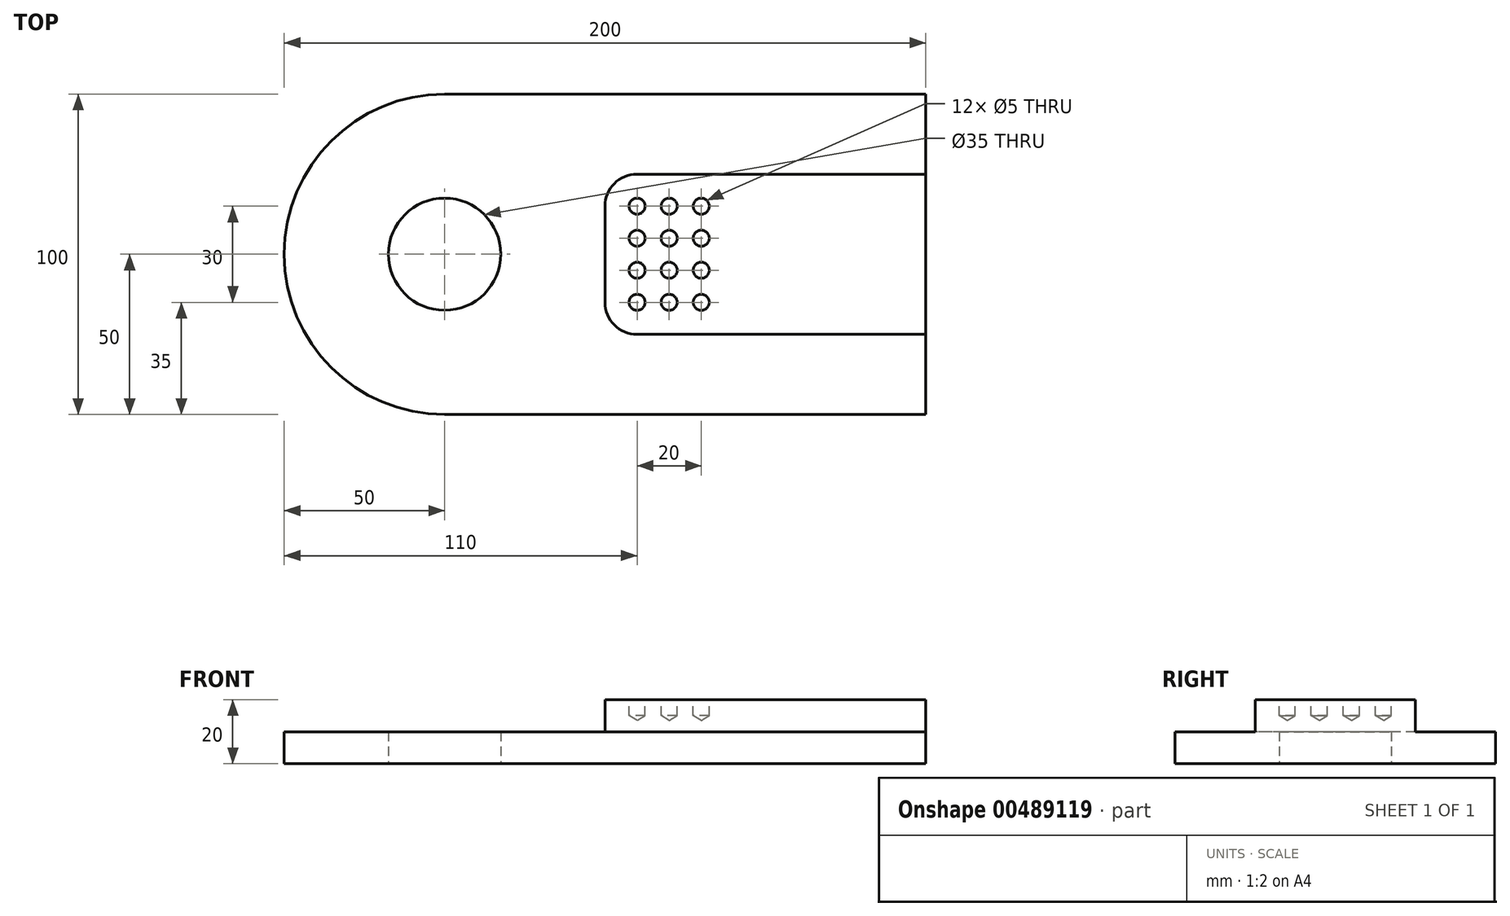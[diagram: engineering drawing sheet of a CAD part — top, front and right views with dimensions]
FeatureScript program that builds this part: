
annotation { "Feature Type Name" : "Feature", "Feature Type Description" : "" }
export const myFeature = defineFeature(function(context is Context, id is Id, definition is map)
    precondition{}
    {
        {
            var Q0;
            Q0=qCreatedBy(makeId("Top.planeOp"),FACE);
            var sketch = newSketch(context, id + "F0", { "sketchPlane" : qUnion([Q0])});
            skCircle(sketch, "E0", {"center": v(0, 0) * mm, "radius": 17.5 * mm});
            skArc(sketch, "E1", {"start": v(0, 50) * mm, "mid": v(-50, 0) * mm, "end": v(0, -50) * mm});
            skLineSegment(sketch, "E2.bottom", {"start": v(0, 50) * mm, "end": v(150, 50) * mm});
            skLineSegment(sketch, "E2.top", {"start": v(0, -50) * mm, "end": v(150, -50) * mm});
            skLineSegment(sketch, "E2.left", {"start": v(0, 50) * mm, "end": v(0, -50) * mm});
            skLineSegment(sketch, "E2.right", {"start": v(150, 50) * mm, "end": v(150, -50) * mm});
            skSolve(sketch);
        }
        {
            var Q0;
            Q0 = qSketchRegion(id + "F0", true);
            extrude(context, id + "F1", {"entities" : qUnion([Q0]), "depth" : 10 * mm});
        }
        {
            var Q0;
            Q0=makeQuery(id+"F1.opExtrude","CAP_FACE",FACE,{"disambiguationData":[OSD([sQuery(id+"F0.wireOp",EDGE,"E0"),sQuery(id+"F0.wireOp",EDGE,"E1"),sQuery(id+"F0.wireOp",EDGE,"E2.bottom"),sQuery(id+"F0.wireOp",EDGE,"E2.top"),sQuery(id+"F0.wireOp",EDGE,"E2.right")])],"isStart":false});
            var sketch = newSketch(context, id + "F2", { "sketchPlane" : qUnion([Q0])});
            skLineSegment(sketch, "E3.bottom", {"start": v(150, 25) * mm, "end": v(60, 25) * mm});
            skLineSegment(sketch, "E3.top", {"start": v(150, -25) * mm, "end": v(60, -25) * mm});
            skLineSegment(sketch, "E3.left", {"start": v(150, 25) * mm, "end": v(150, -25) * mm});
            skLineSegment(sketch, "E3.right", {"start": v(50, 15) * mm, "end": v(50, -15) * mm});
            skPoint(sketch, "E4.visualSharp", {"position": v(50, 25) * mm});
            skArc(sketch, "E4.filletArc", {"start": v(60, 25) * mm, "mid": v(52.93, 22.07) * mm, "end": v(50, 15) * mm});
            skPoint(sketch, "E5.visualSharp", {"position": v(50, -25) * mm});
            skArc(sketch, "E5.filletArc", {"start": v(50, -15) * mm, "mid": v(52.93, -22.07) * mm, "end": v(60, -25) * mm});
            skSolve(sketch);
        }
        {
            var Q0;
            Q0 = qSketchRegion(id + "F2", true);
            extrude(context, id + "F3", {"entities" : qUnion([Q0]), "operationType" : NewBodyOperationType.ADD, "depth" : 10 * mm});
        }
        {
            var Q0;
            Q0=makeQuery(id+"F3.opExtrude","CAP_FACE",FACE,{"disambiguationData":[OSD([sQuery(id+"F2.wireOp",EDGE,"E3.bottom"),sQuery(id+"F2.wireOp",EDGE,"E3.top"),sQuery(id+"F2.wireOp",EDGE,"E3.left"),sQuery(id+"F2.wireOp",EDGE,"E3.right"),sQuery(id+"F2.wireOp",EDGE,"E4.filletArc"),sQuery(id+"F2.wireOp",EDGE,"E5.filletArc")])],"isStart":false});
            var sketch = newSketch(context, id + "F4", { "sketchPlane" : qUnion([Q0])});
            skPoint(sketch, "E6", {"position": v(60, 15) * mm});
            skPoint(sketch, "E7.0.1.0", {"position": v(60, 5) * mm});
            skPoint(sketch, "E7.0.2.0", {"position": v(60, -5) * mm});
            skPoint(sketch, "E7.0.3.0", {"position": v(60, -15) * mm});
            skPoint(sketch, "E7.1.0.0", {"position": v(70, 15) * mm});
            skPoint(sketch, "E7.1.1.0", {"position": v(70, 5) * mm});
            skPoint(sketch, "E7.1.2.0", {"position": v(70, -5) * mm});
            skPoint(sketch, "E7.1.3.0", {"position": v(70, -15) * mm});
            skPoint(sketch, "E7.2.0.0", {"position": v(80, 15) * mm});
            skPoint(sketch, "E7.2.1.0", {"position": v(80, 5) * mm});
            skPoint(sketch, "E7.2.2.0", {"position": v(80, -5) * mm});
            skPoint(sketch, "E7.2.3.0", {"position": v(80, -15) * mm});
            skLineSegment(sketch, "E7.direction1", {"start": v(60, 15) * mm, "end": v(70, 15) * mm, "construction": true});
            skLineSegment(sketch, "E7.direction2", {"start": v(60, 15) * mm, "end": v(60, 5) * mm, "construction": true});
            skSolve(sketch);
        }
        {
            var Q0;
            Q0=sQuery(id+"F4.wireOp",VERTEX,"E6");
            var Q1;
            Q1=sQuery(id+"F4.wireOp",VERTEX,"E7.1.0.0");
            var Q2;
            Q2=sQuery(id+"F4.wireOp",VERTEX,"E7.2.0.0");
            var Q3;
            Q3=sQuery(id+"F4.wireOp",VERTEX,"E7.0.1.0");
            var Q4;
            Q4=sQuery(id+"F4.wireOp",VERTEX,"E7.1.1.0");
            var Q5;
            Q5=sQuery(id+"F4.wireOp",VERTEX,"E7.2.1.0");
            var Q6;
            Q6=sQuery(id+"F4.wireOp",VERTEX,"E7.0.2.0");
            var Q7;
            Q7=sQuery(id+"F4.wireOp",VERTEX,"E7.1.2.0");
            var Q8;
            Q8=sQuery(id+"F4.wireOp",VERTEX,"E7.2.2.0");
            var Q9;
            Q9=sQuery(id+"F4.wireOp",VERTEX,"E7.0.3.0");
            var Q10;
            Q10=sQuery(id+"F4.wireOp",VERTEX,"E7.1.3.0");
            var Q11;
            Q11=sQuery(id+"F4.wireOp",VERTEX,"E7.2.3.0");
            var Q12;
            Q12=makeQuery(id+"F1.opExtrude","SWEPT_BODY",BODY,{"disambiguationData":[OSD([sQuery(id+"F0.wireOp",EDGE,"E0"),sQuery(id+"F0.wireOp",EDGE,"E1"),sQuery(id+"F0.wireOp",EDGE,"E2.bottom"),sQuery(id+"F0.wireOp",EDGE,"E2.top"),sQuery(id+"F0.wireOp",EDGE,"E2.right")])]});
            hole(context, id + "F5", {"style" : HoleStyle.SIMPLE, "endStyle" : HoleEndStyle.BLIND, "holeDiameter" : 5 * mm, "holeDepth" : 5 * mm, "isTappedThrough" : true, "tappedDepth" : 12 * mm, "tapClearance" : 3, "locations" : qUnion([Q0, Q1, Q2, Q3, Q4, Q5, Q6, Q7, Q8, Q9, Q10, Q11]), "scope" : qUnion([Q12])});
        }
        {
            var Q0;
            Q0=qCreatedBy(makeId("Top.planeOp"),FACE);
            var sketch = newSketch(context, id + "F6", { "sketchPlane" : qUnion([Q0])});
            skLineSegment(sketch, "E8.bottom", {"start": v(-55, 55) * mm, "end": v(155, 55) * mm});
            skLineSegment(sketch, "E8.top", {"start": v(-55, -55) * mm, "end": v(155, -55) * mm});
            skLineSegment(sketch, "E8.left", {"start": v(-55, 55) * mm, "end": v(-55, -55) * mm});
            skLineSegment(sketch, "E8.right", {"start": v(155, 55) * mm, "end": v(155, -55) * mm});
            skSolve(sketch);
        }
        {
            var Q0;
            Q0=makeQuery(id+"F6.imprint","IMPRINT",FACE,{"disambiguationData":[TD([[makeQuery(id+"F6.imprint","IMPRINT",EDGE,{"derivedFrom":sQuery(id+"F6.wireOp",EDGE,"E8.bottom")}),-1.0]])]});
            var sketch = newSketch(context, id + "F7", { "sketchPlane" : qUnion([Q0])});
            skPoint(sketch, "E9", {"position": v(-150, -150) * mm});
            skSolve(sketch);
        }
        {
            var Q0;
            Q0=makeQuery(id+"F7.imprint","IMPRINT",FACE,{"disambiguationData":[TD([[makeQuery(id+"F7.imprint","IMPRINT",EDGE,{"derivedFrom":makeQuery(id+"F6.imprint","IMPRINT",EDGE,{"derivedFrom":sQuery(id+"F6.wireOp",EDGE,"E8.bottom")})}),-1.0]])]});
            cPlane(context, id + "F8", {"entities" : qUnion([Q0]), "cplaneType" : CPlaneType.OFFSET, "offset" : 25 * mm, "width" : 150 * mm, "height" : 150 * mm});
        }
    });
